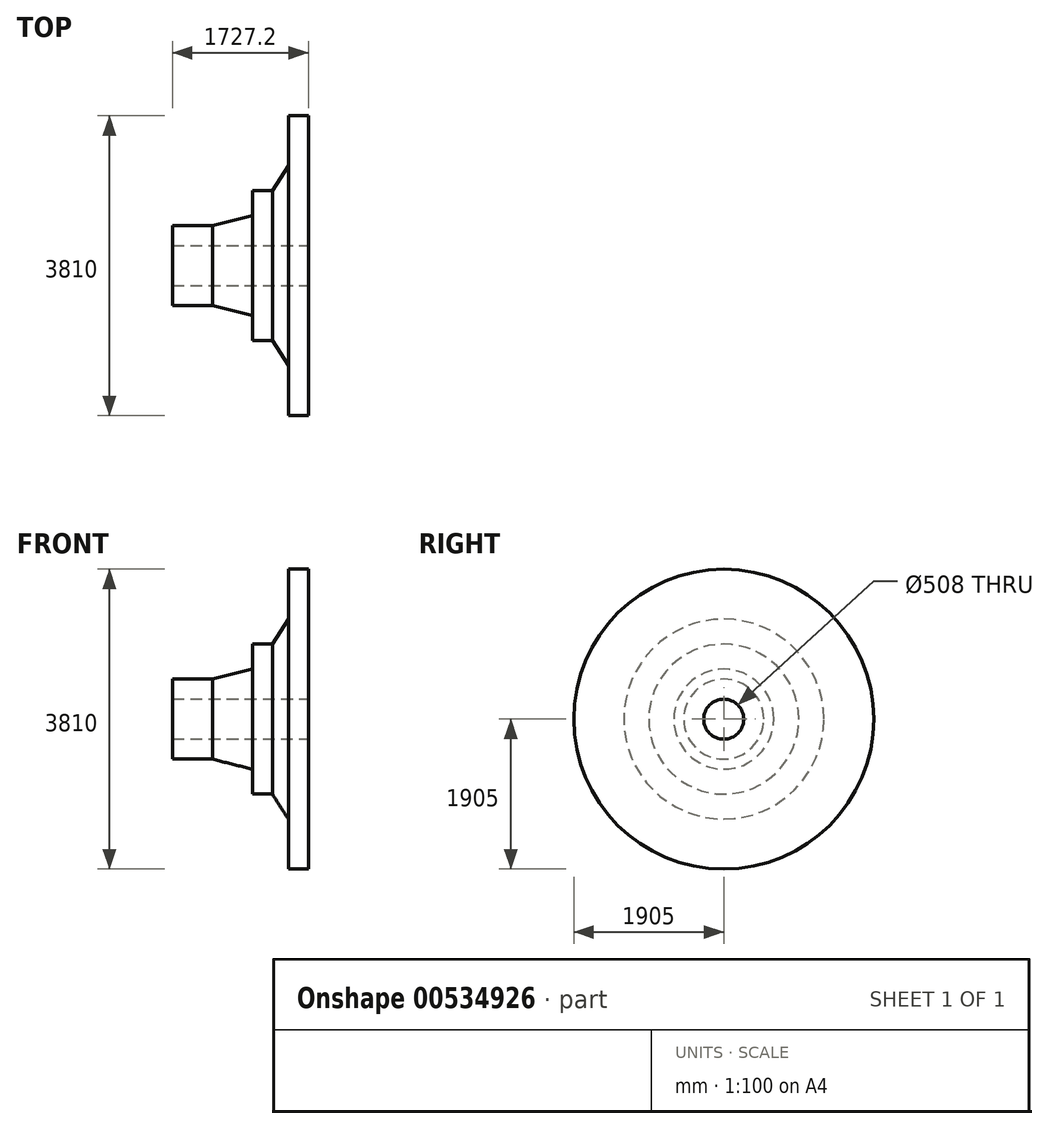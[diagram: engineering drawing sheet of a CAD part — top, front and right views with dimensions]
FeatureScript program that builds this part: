
annotation { "Feature Type Name" : "Feature", "Feature Type Description" : "" }
export const myFeature = defineFeature(function(context is Context, id is Id, definition is map)
    precondition{}
    {
        {
            var Q0;
            Q0=qCreatedBy(makeId("Front.planeOp"),FACE);
            var sketch = newSketch(context, id + "F0", { "sketchPlane" : qUnion([Q0])});
            skLineSegment(sketch, "E0", {"start": v(0, 0) * mm, "end": v(-2711.62, 0) * mm});
            skLineSegment(sketch, "E1", {"start": v(0, 315.78) * mm, "end": v(0, 1905) * mm});
            skLineSegment(sketch, "E2", {"start": v(0, 1905) * mm, "end": v(-254, 1905) * mm});
            skLineSegment(sketch, "E3", {"start": v(-254, 1905) * mm, "end": v(-254, 1270) * mm});
            skLineSegment(sketch, "E4", {"start": v(-254, 1270) * mm, "end": v(-457.2, 952.5) * mm});
            skLineSegment(sketch, "E5", {"start": v(-457.2, 952.5) * mm, "end": v(-711.2, 952.5) * mm});
            skLineSegment(sketch, "E6", {"start": v(-711.2, 952.5) * mm, "end": v(-711.2, 635) * mm});
            skLineSegment(sketch, "E7", {"start": v(-711.2, 635) * mm, "end": v(-1219.2, 508) * mm});
            skLineSegment(sketch, "E8", {"start": v(-1219.2, 508) * mm, "end": v(-1727.2, 508) * mm});
            skLineSegment(sketch, "E9", {"start": v(-1727.2, 508) * mm, "end": v(-1727.2, 254) * mm});
            skLineSegment(sketch, "E10", {"start": v(-1727.2, 254) * mm, "end": v(0, 254) * mm});
            skLineSegment(sketch, "E11", {"start": v(0, 254) * mm, "end": v(0, 1905) * mm});
            skSolve(sketch);
        }
        {
            var Q0;
            Q0 = qSketchRegion(id + "F0", true);
            var Q1;
            Q1=sQuery(id+"F0.wireOp",EDGE,"E0");
            revolve(context, id + "F1", {"entities" : qUnion([Q0]), "axis" : qUnion([Q1]), "revolveType" : RevolveType.FULL});
        }
    });
